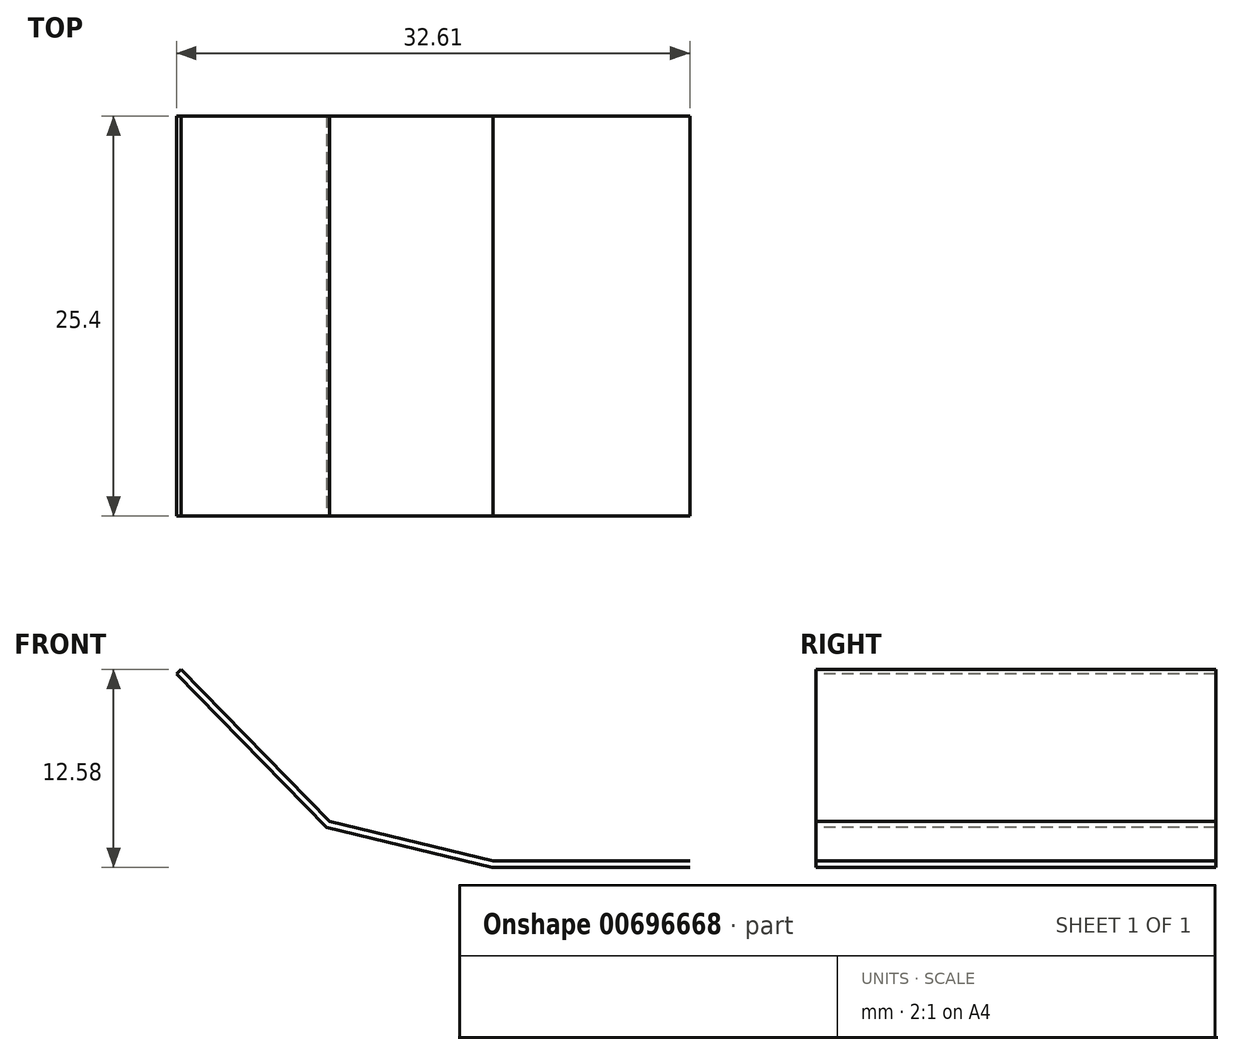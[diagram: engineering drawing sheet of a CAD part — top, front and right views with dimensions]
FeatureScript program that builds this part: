
annotation { "Feature Type Name" : "Feature", "Feature Type Description" : "" }
export const myFeature = defineFeature(function(context is Context, id is Id, definition is map)
    precondition{}
    {
        {
            var Q0;
            Q0=qCreatedBy(makeId("Front.planeOp"),FACE);
            var sketch = newSketch(context, id + "F0", { "sketchPlane" : qUnion([Q0])});
            skLineSegment(sketch, "E0", {"start": v(0, -12.58) * mm, "end": v(-12.58, -12.58) * mm});
            skLineSegment(sketch, "E1", {"start": v(-12.58, -12.58) * mm, "end": v(-23.08, -10.05) * mm});
            skLineSegment(sketch, "E2", {"start": v(-23.08, -10.05) * mm, "end": v(-32.6, -0.28) * mm});
            skLineSegment(sketch, "E3", {"start": v(-32.6, -0.28) * mm, "end": v(-32.32, 0) * mm});
            skLineSegment(sketch, "E4", {"start": v(-32.32, 0) * mm, "end": v(-22.89, -9.66) * mm});
            skLineSegment(sketch, "E5", {"start": v(-22.89, -9.66) * mm, "end": v(-12.5, -12.17) * mm});
            skLineSegment(sketch, "E6", {"start": v(-12.5, -12.17) * mm, "end": v(0, -12.17) * mm});
            skSolve(sketch);
        }
        {
            var Q0;
            Q0=sQuery(id+"F0.wireOp",EDGE,"E6");
            extrude(context, id + "F1", {"bodyType" : ToolBodyType.SURFACE, "surfaceEntities" : qUnion([Q0]), "depth" : 25.4 * mm, "offsetDistance" : 25.4 * mm});
        }
        {
            var Q0;
            Q0=sQuery(id+"F0.wireOp",EDGE,"E5");
            extrude(context, id + "F2", {"bodyType" : ToolBodyType.SURFACE, "surfaceEntities" : qUnion([Q0]), "depth" : 25.4 * mm, "offsetDistance" : 25.4 * mm});
        }
        {
            var Q0;
            Q0=sQuery(id+"F0.wireOp",EDGE,"E0");
            extrude(context, id + "F3", {"bodyType" : ToolBodyType.SURFACE, "surfaceEntities" : qUnion([Q0]), "depth" : 25.4 * mm, "offsetDistance" : 25.4 * mm});
        }
        {
            var Q0;
            Q0=sQuery(id+"F0.wireOp",EDGE,"E1");
            extrude(context, id + "F4", {"bodyType" : ToolBodyType.SURFACE, "surfaceEntities" : qUnion([Q0]), "depth" : 25.4 * mm, "offsetDistance" : 25.4 * mm});
        }
        {
            var Q0;
            Q0=sQuery(id+"F0.wireOp",EDGE,"E4");
            extrude(context, id + "F5", {"bodyType" : ToolBodyType.SURFACE, "surfaceEntities" : qUnion([Q0]), "depth" : 25.4 * mm, "offsetDistance" : 25.4 * mm});
        }
        {
            var Q0;
            Q0=sQuery(id+"F0.wireOp",EDGE,"E2");
            extrude(context, id + "F6", {"bodyType" : ToolBodyType.SURFACE, "surfaceEntities" : qUnion([Q0]), "depth" : 25.4 * mm, "offsetDistance" : 25.4 * mm});
        }
        {
            var Q0;
            Q0=sQuery(id+"F0.wireOp",EDGE,"E3");
            extrude(context, id + "F7", {"bodyType" : ToolBodyType.SURFACE, "surfaceEntities" : qUnion([Q0]), "depth" : 25.4 * mm, "offsetDistance" : 25.4 * mm});
        }
    });
